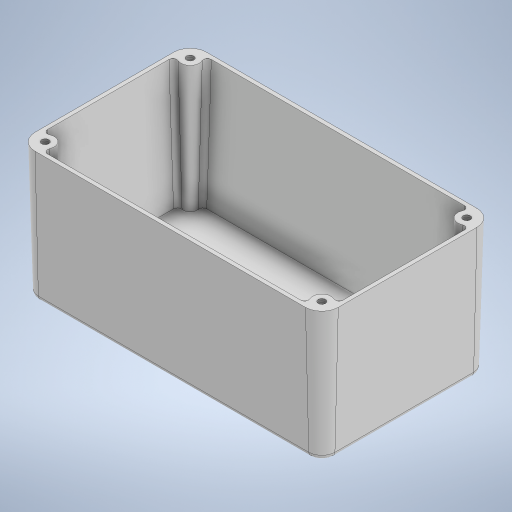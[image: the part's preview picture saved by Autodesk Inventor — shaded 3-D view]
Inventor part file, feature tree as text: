
AUTODESK INVENTOR PART (.ipt)
format: ipt  version: 2023 (Build 270158030, 158C)  size: 504,320 bytes
history: native  units: mm
features: sketch x8, extrude x6, other x4, fillet x3, hole x2, plane x1
ambient origin geometry x8: Origin, YZ Plane, XZ Plane, XY Plane, X Axis, Y Axis, Z Axis, Center Point
bodies: Body1 (feature_tree), Body2 (feature_tree)
feature tree (24):
  other  "Die Cast Box"
  other  "Annotations"
  extrude  "Extrusion1"  Depth=63.6mm
  sketch  "Sketch2"  dims[d2=5.0mm d10=51.1mm d11=0.261799mm]
  plane  "Work Plane1"
  extrude  "Extrusion2"  Depth=5.0mm
  extrude  "Extrusion3"  Depth=1.5mm
  fillet  "Fillet1"  Radius=1.5mm
  sketch  "Sketch4"  dims[d16=4.0mm d17=-1.5mm d18=51.1mm d19=-0.261799mm]
  fillet  "Fillet2"  Radius=1.5mm
  hole  "Hole1"  [1 undecoded]
  extrude  "Extrusion4"  Depth=4.0mm
  fillet  "Fillet3"  Radius=5.3mm
  hole  "Hole2"  [1 undecoded]
  extrude  "Extrusion5"  Depth=3.8mm
  extrude  "Extrusion6"  Depth=1.5mm
  sketch  "Sketch1"  dims[d0=114.5mm d1=63.6mm]
  sketch  "Sketch3"  dims[d12=1.5mm d13=1.5mm d14=1.5mm d15=1.5mm]
  sketch  "Sketch5"  dims[d20=4.0mm d21=4.0mm d22=5.3mm]
  other  "Die Cast Lid"
  sketch  "Sketch6"  dims[d23=3.8mm d24=3.8mm]
  sketch  "Sketch7"  dims[d25=3.8mm d26=3.8mm]
  sketch  "Sketch8"  dims[d27=10.0mm d28=0.174533mm d29=1.5mm d30=3.0mm d31=2.0mm d32=2.85mm d33=7.0mm d34=4.0mm d35=2.0mm d36=90.0deg d37=20.0mm d38=20.594885mm d39=5.67mm d40=4.0mm d41=0.0mm d42=1.5mm d43=3.0mm d44=3.0mm d45=7.0mm d46=4.0mm d47=2.0mm d48=90.0deg d49=4.0mm d50=20.594885mm d51=0.5mm d52=0.5mm d53=0.5mm d54=0.5mm d55=1.5mm d56=1.5mm d57=1.5mm d58=1.5mm d59=0.5mm d60=0.5mm d62=10.0mm d63=10.0mm d64=10.0mm d65=10.0mm d66=2.5mm d67=0.0mm d71=9.0mm d72=9.0mm d73=9.0mm d74=9.0mm d75=1.0mm d76=2.5mm d77=0.0mm]
  other  "General Note 1"
note: 2 required parameter values undecoded (feature->parameter linkage not recoverable at this tier; creation-order binding heuristic only, values carry confidence <= 0.55)
